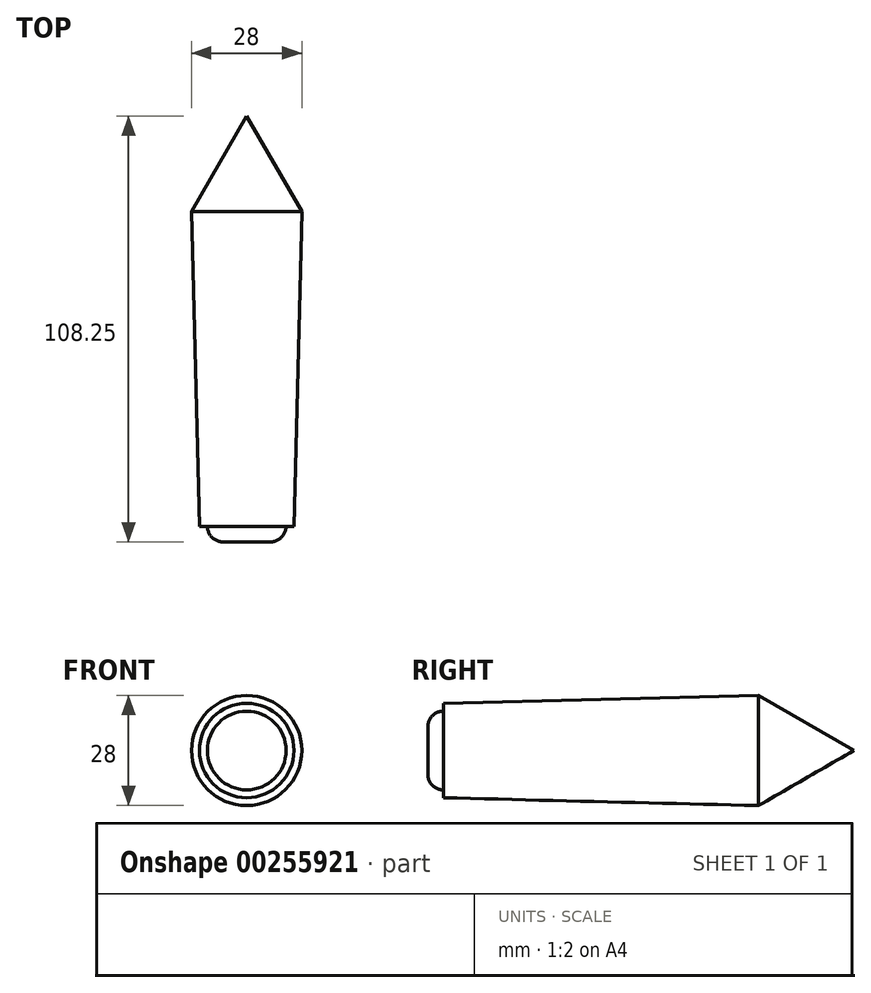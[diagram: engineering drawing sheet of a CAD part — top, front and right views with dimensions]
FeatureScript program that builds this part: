
annotation { "Feature Type Name" : "Feature", "Feature Type Description" : "" }
export const myFeature = defineFeature(function(context is Context, id is Id, definition is map)
    precondition{}
    {
        {
            var Q0;
            Q0=qCreatedBy(makeId("Top.planeOp"),FACE);
            var sketch = newSketch(context, id + "F0", { "sketchPlane" : qUnion([Q0])});
            skLineSegment(sketch, "E0", {"start": v(0, 53.58) * mm, "end": v(14, 29.33) * mm});
            skLineSegment(sketch, "E1", {"start": v(14, 29.33) * mm, "end": v(12, -50.72) * mm});
            skLineSegment(sketch, "E2", {"start": v(12, -50.72) * mm, "end": v(10, -50.67) * mm});
            skLineSegment(sketch, "E3", {"start": v(10, -50.67) * mm, "end": v(10, -54.67) * mm});
            skLineSegment(sketch, "E4", {"start": v(10, -54.67) * mm, "end": v(0, -54.67) * mm});
            skLineSegment(sketch, "E5", {"start": v(0, -54.67) * mm, "end": v(0, 53.58) * mm});
            skSolve(sketch);
        }
        {
            var Q0;
            Q0=makeQuery(id+"F0.imprint","IMPRINT",FACE,{"disambiguationData":[TD([[makeQuery(id+"F0.imprint","IMPRINT",EDGE,{"derivedFrom":sQuery(id+"F0.wireOp",EDGE,"E0")}),-1.0]])]});
            var Q1;
            Q1=sQuery(id+"F0.wireOp",EDGE,"E5");
            revolve(context, id + "F1", {"entities" : qUnion([Q0]), "axis" : qUnion([Q1]), "revolveType" : RevolveType.FULL});
        }
        {
            var Q0;
            Q0=makeQuery(id+"F1.opRevolve","SWEPT_EDGE",EDGE,{"disambiguationData":[OSD([sQuery(id+"F0.wireOp",EDGE,"E3"),sQuery(id+"F0.wireOp",EDGE,"E4")])]});
            fillet(context, id + "F2", {"entities" : qUnion([Q0]), "radius" : 4 * mm, "tangentPropagation" : true, "allowEdgeOverflow" : false});
        }
    });
